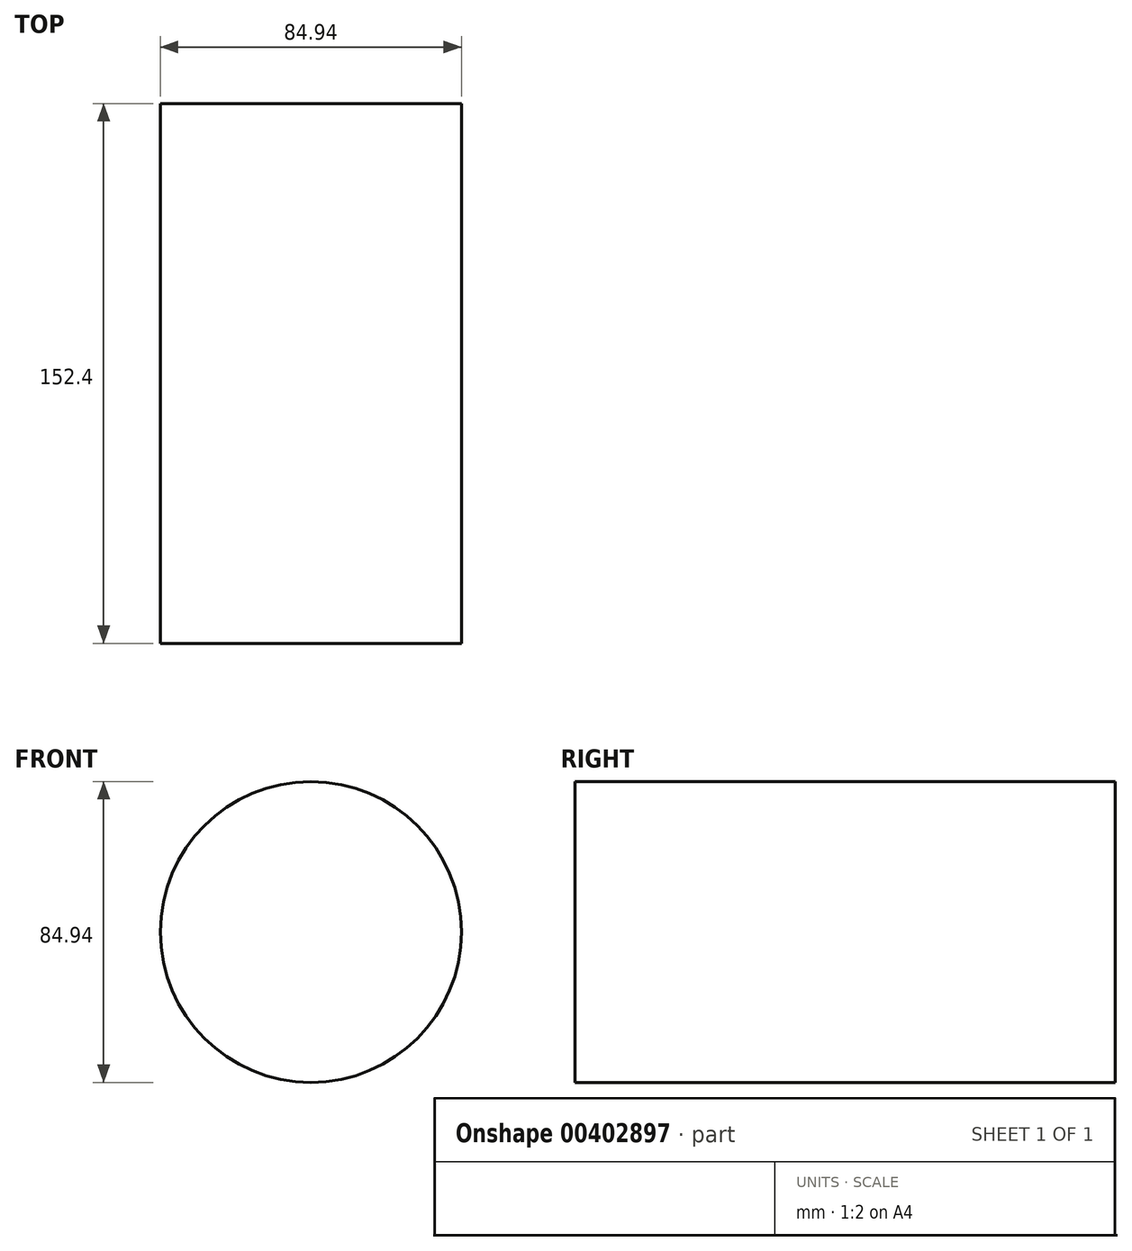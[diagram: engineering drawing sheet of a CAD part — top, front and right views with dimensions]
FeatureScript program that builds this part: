
annotation { "Feature Type Name" : "Feature", "Feature Type Description" : "" }
export const myFeature = defineFeature(function(context is Context, id is Id, definition is map)
    precondition{}
    {
        {
            var Q0;
            Q0=qCreatedBy(makeId("Front.planeOp"),FACE);
            var sketch = newSketch(context, id + "F0", { "sketchPlane" : qUnion([Q0])});
            skCircle(sketch, "E0", {"center": v(0, 0) * mm, "radius": 42.47 * mm});
            skSolve(sketch);
        }
        {
            var Q0;
            Q0 = qSketchRegion(id + "F0", true);
            extrude(context, id + "F1", {"entities" : qUnion([Q0]), "depth" : 152.4 * mm});
        }
    });
